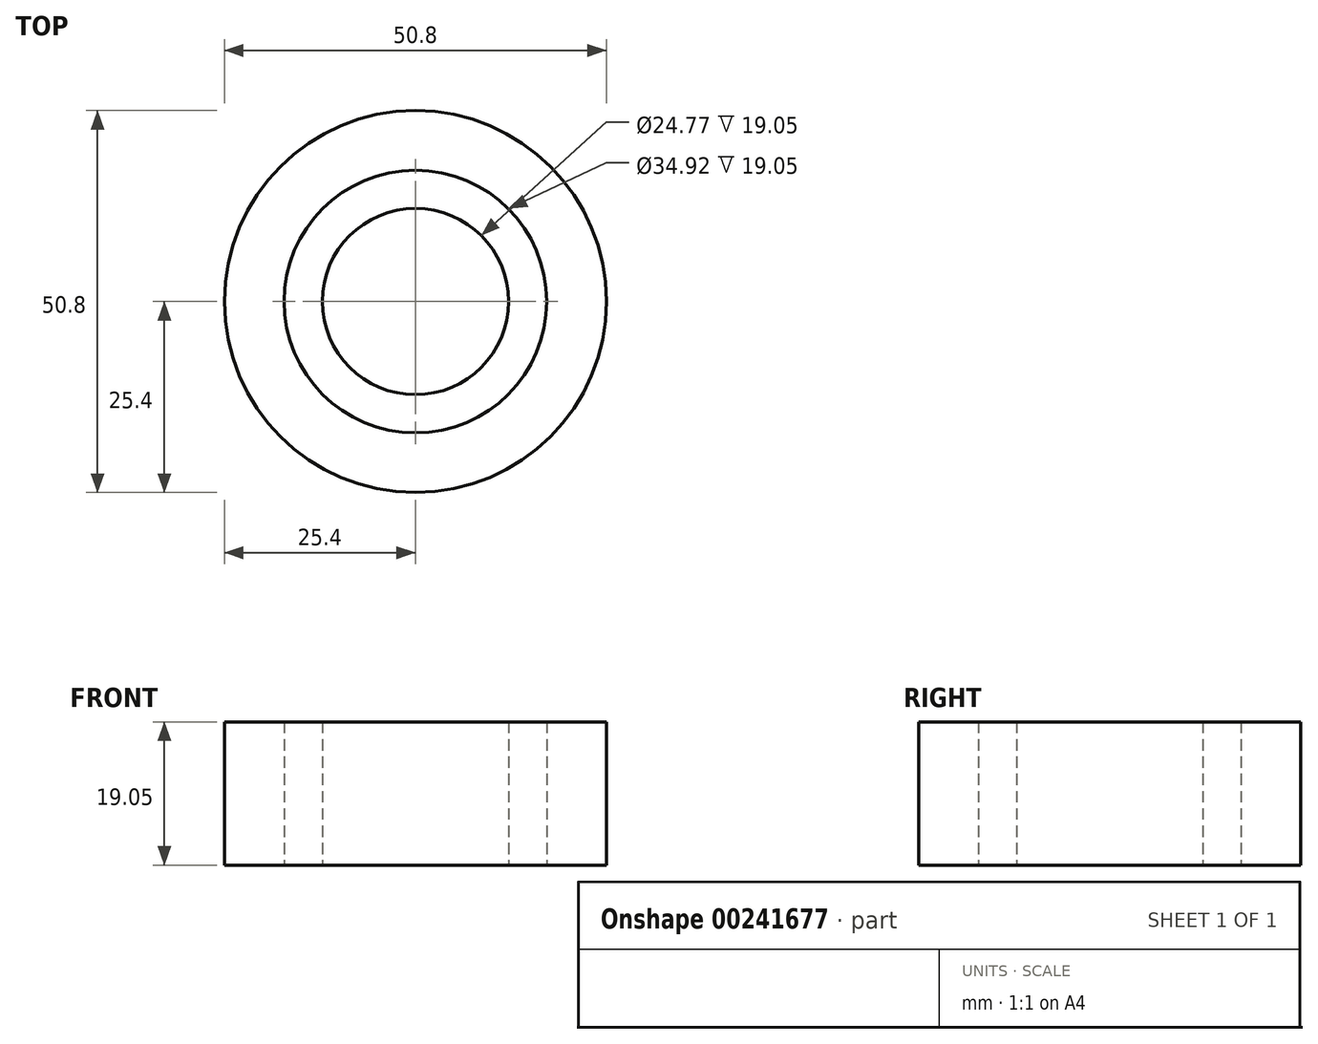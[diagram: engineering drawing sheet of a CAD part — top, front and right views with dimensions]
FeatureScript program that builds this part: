
annotation { "Feature Type Name" : "Feature", "Feature Type Description" : "" }
export const myFeature = defineFeature(function(context is Context, id is Id, definition is map)
    precondition{}
    {
        {
            var Q0;
            Q0=qCreatedBy(makeId("Top.planeOp"),FACE);
            var sketch = newSketch(context, id + "F0", { "sketchPlane" : qUnion([Q0])});
            skCircle(sketch, "E0", {"center": v(0, 0) * mm, "radius": 25.4 * mm});
            skCircle(sketch, "E1", {"center": v(0, 0) * mm, "radius": 17.46 * mm});
            skSolve(sketch);
        }
        {
            var Q0;
            Q0 = qSketchRegion(id + "F0", true);
            extrude(context, id + "F1", {"entities" : qUnion([Q0]), "depth" : 19.05 * mm});
        }
        {
            var Q0;
            Q0=qCreatedBy(makeId("Top.planeOp"),FACE);
            var sketch = newSketch(context, id + "F2", { "sketchPlane" : qUnion([Q0])});
            skPoint(sketch, "E2.0", {"position": v(0, 0) * mm});
            skCircle(sketch, "E3.0", {"center": v(0, 0) * mm, "radius": 17.46 * mm});
            skCircle(sketch, "E4.0", {"center": v(0, 0) * mm, "radius": 12.38 * mm});
            skSolve(sketch);
        }
        {
            var Q0;
            Q0 = qSketchRegion(id + "F2", true);
            extrude(context, id + "F3", {"entities" : qUnion([Q0]), "depth" : 19.05 * mm});
        }
    });
